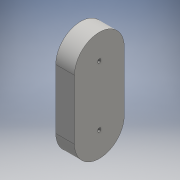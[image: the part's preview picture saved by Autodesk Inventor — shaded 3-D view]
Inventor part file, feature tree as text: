
AUTODESK INVENTOR PART (.ipt)
format: ipt  version: 2016 (Build 200138000, 138)  size: 133,632 bytes
history: native  units: mm
features: sketch x9, extrude x3, hole x2, other x1
ambient origin geometry x8: Origin, YZ Plane, XZ Plane, XY Plane, X Axis, Y Axis, Z Axis, Center Point
bodies: Body1 (feature_tree)
feature tree (15):
  other  "Bryła1"
  sketch  "Szkic1"
  sketch  "Szkic 3D1"
  extrude  "Wyciągnięcie proste1"  Depth=24.0mm
  sketch  "Szkic2"
  sketch  "Szkic 3D2"
  sketch  "Szkic 3D3"
  extrude  "Wyciągnięcie proste2"  Depth=48.0mm
  sketch  "Szkic3"
  sketch  "Szkic 3D4"
  hole  "Otwór1"  [1 undecoded]
  hole  "Otwór2"  [1 undecoded]
  extrude  "Wyciągnięcie proste3"  Depth=15.0mm TaperAngle=0.0deg
  sketch  "Szkic4"
  sketch  "Szkic5"
note: 2 required parameter values undecoded (feature->parameter linkage not recoverable at this tier; creation-order binding heuristic only, values carry confidence <= 0.55)
